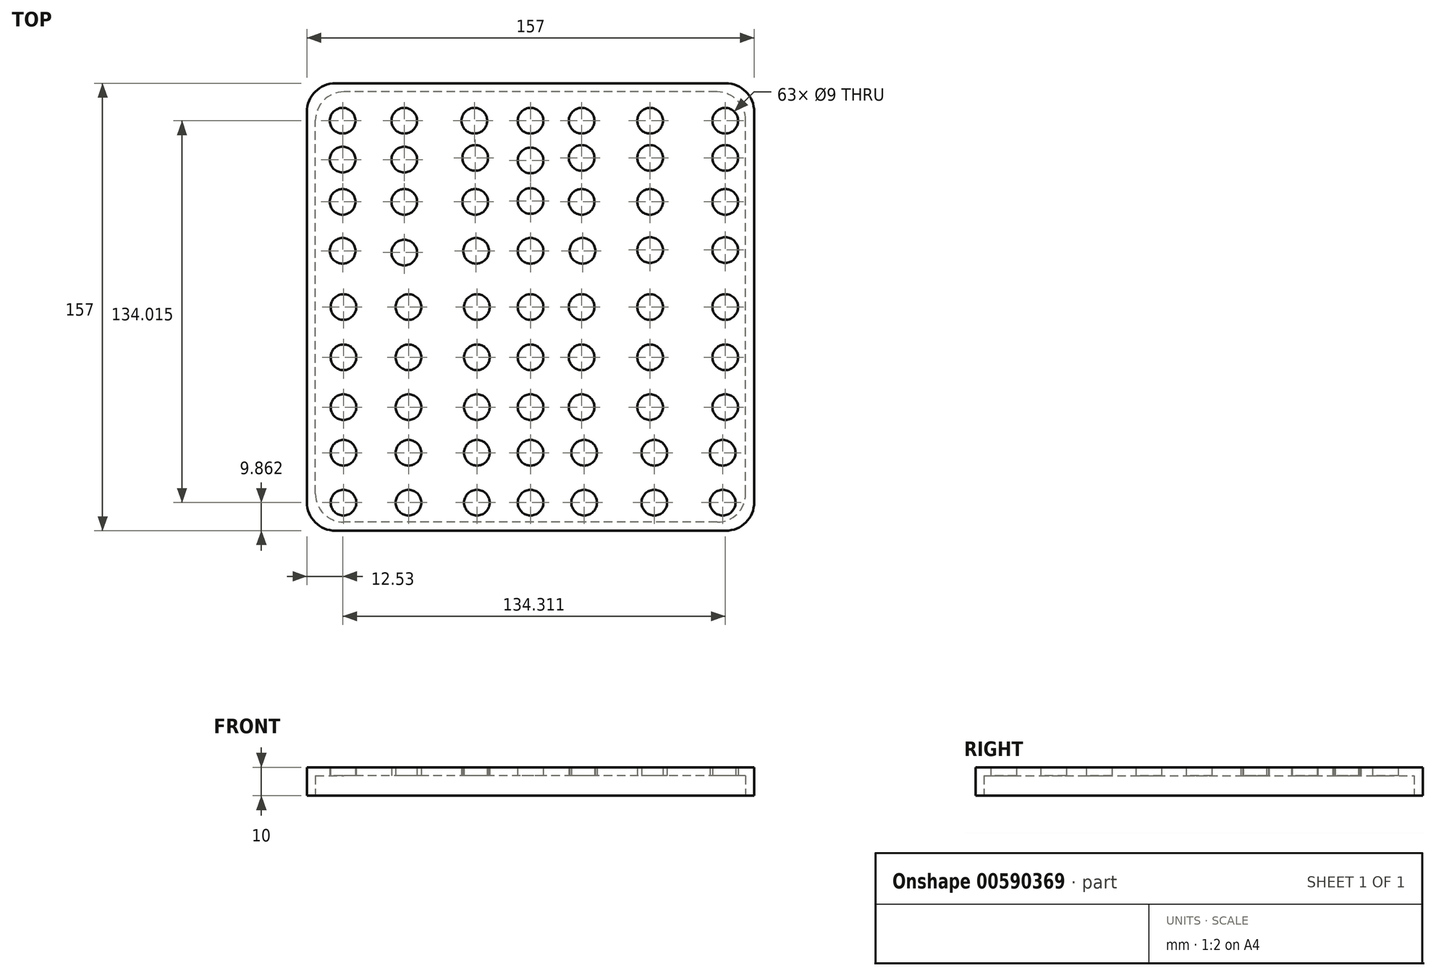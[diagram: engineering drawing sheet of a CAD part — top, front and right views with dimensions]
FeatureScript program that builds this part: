
annotation { "Feature Type Name" : "Feature", "Feature Type Description" : "" }
export const myFeature = defineFeature(function(context is Context, id is Id, definition is map)
    precondition{}
    {
        {
            var Q0;
            Q0=qCreatedBy(makeId("Top.planeOp"),FACE);
            var sketch = newSketch(context, id + "F0", { "sketchPlane" : qUnion([Q0])});
            skLineSegment(sketch, "E0.bottom", {"start": v(78.5, 78.5) * mm, "end": v(-78.5, 78.5) * mm});
            skLineSegment(sketch, "E0.top", {"start": v(78.5, -78.5) * mm, "end": v(-78.5, -78.5) * mm});
            skLineSegment(sketch, "E0.left", {"start": v(78.5, 78.5) * mm, "end": v(78.5, -78.5) * mm});
            skLineSegment(sketch, "E0.right", {"start": v(-78.5, 78.5) * mm, "end": v(-78.5, -78.5) * mm});
            skPoint(sketch, "E0.middle", {"position": v(0, 0) * mm});
            skSolve(sketch);
        }
        {
            var Q0;
            Q0=qSketchRegion(id+"F0",true);
            extrude(context, id + "F1", {"entities" : qUnion([Q0]), "depth" : 10 * mm, "offsetDistance" : 25 * mm});
        }
        {
            var Q0;
            Q0=qCreatedBy(makeId("Top.planeOp"),FACE);
            var sketch = newSketch(context, id + "F2", { "sketchPlane" : qUnion([Q0])});
            skLineSegment(sketch, "E1.bottom", {"start": v(75.5, -75.5) * mm, "end": v(-75.5, -75.5) * mm});
            skLineSegment(sketch, "E1.top", {"start": v(75.5, 75.5) * mm, "end": v(-75.5, 75.5) * mm});
            skLineSegment(sketch, "E1.left", {"start": v(75.5, -75.5) * mm, "end": v(75.5, 75.5) * mm});
            skLineSegment(sketch, "E1.right", {"start": v(-75.5, -75.5) * mm, "end": v(-75.5, 75.5) * mm});
            skSolve(sketch);
        }
        {
            var Q0;
            Q0=qSketchRegion(id+"F2",true);
            extrude(context, id + "F3", {"entities" : qUnion([Q0]), "operationType" : NewBodyOperationType.REMOVE, "depth" : 7 * mm, "offsetDistance" : 25 * mm});
        }
        {
            var Q0;
            Q0=qCreatedBy(makeId("Top.planeOp"),FACE);
            var sketch = newSketch(context, id + "F4", { "sketchPlane" : qUnion([Q0])});
            skPoint(sketch, "E2", {"position": v(0, 0) * mm});
            skPoint(sketch, "E3", {"position": v(0, 19.72) * mm});
            skPoint(sketch, "E4", {"position": v(0, 51.44) * mm});
            skPoint(sketch, "E5", {"position": v(0, 65.38) * mm});
            skPoint(sketch, "E6", {"position": v(0, 37.2) * mm});
            skPoint(sketch, "E7", {"position": v(17.94, 0) * mm});
            skPoint(sketch, "E8", {"position": v(41.95, 0) * mm});
            skPoint(sketch, "E9", {"position": v(68.34, 0) * mm});
            skPoint(sketch, "E10", {"position": v(-18.83, 0) * mm});
            skPoint(sketch, "E11", {"position": v(-42.84, 0) * mm});
            skPoint(sketch, "E12", {"position": v(-65.67, 0) * mm});
            skPoint(sketch, "E13", {"position": v(0, -17.64) * mm});
            skPoint(sketch, "E14", {"position": v(0, -35.13) * mm});
            skPoint(sketch, "E15", {"position": v(0, -51.15) * mm});
            skPoint(sketch, "E16", {"position": v(0, -68.64) * mm});
            skPoint(sketch, "E17", {"position": v(-44.33, 36.91) * mm});
            skPoint(sketch, "E18", {"position": v(-65.97, 65.38) * mm});
            skPoint(sketch, "E19", {"position": v(-44.33, 65.38) * mm});
            skPoint(sketch, "E20", {"position": v(-19.72, 65.38) * mm});
            skPoint(sketch, "E21", {"position": v(-44.33, 51.74) * mm});
            skPoint(sketch, "E22", {"position": v(-19.42, 52.33) * mm});
            skPoint(sketch, "E23", {"position": v(-19.42, 36.91) * mm});
            skPoint(sketch, "E24", {"position": v(-19.12, 19.72) * mm});
            skPoint(sketch, "E25", {"position": v(-44.33, 19.12) * mm});
            skPoint(sketch, "E26", {"position": v(-65.97, 36.91) * mm});
            skPoint(sketch, "E27", {"position": v(-65.97, 19.72) * mm});
            skPoint(sketch, "E28", {"position": v(-65.97, 51.74) * mm});
            skPoint(sketch, "E29", {"position": v(68.34, 20.01) * mm});
            skPoint(sketch, "E30", {"position": v(41.95, 20.01) * mm});
            skPoint(sketch, "E31", {"position": v(18.23, 19.72) * mm});
            skPoint(sketch, "E32", {"position": v(17.94, 36.91) * mm});
            skPoint(sketch, "E33", {"position": v(41.95, 36.91) * mm});
            skPoint(sketch, "E34", {"position": v(68.34, 36.91) * mm});
            skPoint(sketch, "E35", {"position": v(17.94, 65.38) * mm});
            skPoint(sketch, "E36", {"position": v(41.95, 65.38) * mm});
            skPoint(sketch, "E37", {"position": v(68.34, 65.38) * mm});
            skPoint(sketch, "E38", {"position": v(17.94, 52.33) * mm});
            skPoint(sketch, "E39", {"position": v(41.95, 52.33) * mm});
            skPoint(sketch, "E40", {"position": v(68.34, 52.33) * mm});
            skPoint(sketch, "E41", {"position": v(-18.83, -17.64) * mm});
            skPoint(sketch, "E42", {"position": v(-42.84, -17.64) * mm});
            skPoint(sketch, "E43", {"position": v(-65.67, -17.64) * mm});
            skPoint(sketch, "E44", {"position": v(-18.83, -35.13) * mm});
            skPoint(sketch, "E45", {"position": v(-42.84, -35.13) * mm});
            skPoint(sketch, "E46", {"position": v(-65.67, -35.13) * mm});
            skPoint(sketch, "E47", {"position": v(-18.83, -51.15) * mm});
            skPoint(sketch, "E48", {"position": v(-42.84, -51.15) * mm});
            skPoint(sketch, "E49", {"position": v(-65.67, -51.15) * mm});
            skPoint(sketch, "E50", {"position": v(-18.83, -68.64) * mm});
            skPoint(sketch, "E51", {"position": v(-42.84, -68.64) * mm});
            skPoint(sketch, "E52", {"position": v(-65.67, -68.64) * mm});
            skPoint(sketch, "E53", {"position": v(17.94, -17.64) * mm});
            skPoint(sketch, "E54", {"position": v(41.95, -17.64) * mm});
            skPoint(sketch, "E55", {"position": v(68.34, -17.64) * mm});
            skPoint(sketch, "E56", {"position": v(17.94, -35.13) * mm});
            skPoint(sketch, "E57", {"position": v(41.95, -35.13) * mm});
            skPoint(sketch, "E58", {"position": v(68.34, -35.13) * mm});
            skPoint(sketch, "E59", {"position": v(18.83, -51.15) * mm});
            skPoint(sketch, "E60", {"position": v(43.44, -51.15) * mm});
            skPoint(sketch, "E61", {"position": v(18.83, -68.64) * mm});
            skPoint(sketch, "E62", {"position": v(43.44, -68.64) * mm});
            skPoint(sketch, "E63", {"position": v(67.45, -51.15) * mm});
            skPoint(sketch, "E64", {"position": v(67.45, -68.64) * mm});
            skSolve(sketch);
        }
        {
            var Q0;
            Q0=sQuery(id+"F4.wireOp",VERTEX,"E2");
            var Q1;
            Q1=sQuery(id+"F4.wireOp",VERTEX,"01be2f64-9275-40fd-adfd-86fc247d9703");
            var Q2;
            Q2=sQuery(id+"F4.wireOp",VERTEX,"E3");
            var Q3;
            Q3=sQuery(id+"F4.wireOp",VERTEX,"E6");
            var Q4;
            Q4=sQuery(id+"F4.wireOp",VERTEX,"E4");
            var Q5;
            Q5=sQuery(id+"F4.wireOp",VERTEX,"E5");
            var Q6;
            Q6=sQuery(id+"F4.wireOp",VERTEX,"E7");
            var Q7;
            Q7=sQuery(id+"F4.wireOp",VERTEX,"7066c532-d9dd-423a-8bff-f60177c8eb84");
            var Q8;
            Q8=sQuery(id+"F4.wireOp",VERTEX,"E8");
            var Q9;
            Q9=sQuery(id+"F4.wireOp",VERTEX,"2cc3d04b-55ef-4e46-9bfc-cd6a145b7dbc");
            var Q10;
            Q10=sQuery(id+"F4.wireOp",VERTEX,"E9");
            var Q11;
            Q11=sQuery(id+"F4.wireOp",VERTEX,"E10");
            var Q12;
            Q12=sQuery(id+"F4.wireOp",VERTEX,"02460886-5748-4483-a859-1664056adb13");
            var Q13;
            Q13=sQuery(id+"F4.wireOp",VERTEX,"E11");
            var Q14;
            Q14=sQuery(id+"F4.wireOp",VERTEX,"182e11dd-57cf-4a7e-8525-31e6d83ff862");
            var Q15;
            Q15=sQuery(id+"F4.wireOp",VERTEX,"E12");
            var Q16;
            Q16=sQuery(id+"F4.wireOp",VERTEX,"E13");
            var Q17;
            Q17=sQuery(id+"F4.wireOp",VERTEX,"E14");
            var Q18;
            Q18=sQuery(id+"F4.wireOp",VERTEX,"22c52a95-364c-45c8-bfcc-b8bc63de801a");
            var Q19;
            Q19=sQuery(id+"F4.wireOp",VERTEX,"E15");
            var Q20;
            Q20=sQuery(id+"F4.wireOp",VERTEX,"c324e29c-9176-4c9c-977c-a24ceaadd785");
            var Q21;
            Q21=sQuery(id+"F4.wireOp",VERTEX,"92aa8679-3bd7-4545-9122-d12983432420");
            var Q22;
            Q22=sQuery(id+"F4.wireOp",VERTEX,"E33");
            var Q23;
            Q23=sQuery(id+"F4.wireOp",VERTEX,"96c0b8bc-8c1f-43fb-ba5c-182eb7d20bf4");
            var Q24;
            Q24=sQuery(id+"F4.wireOp",VERTEX,"E37");
            var Q25;
            Q25=sQuery(id+"F4.wireOp",VERTEX,"E40");
            var Q26;
            Q26=sQuery(id+"F4.wireOp",VERTEX,"E34");
            var Q27;
            Q27=sQuery(id+"F4.wireOp",VERTEX,"c3c9688b-514f-4bd6-b36d-9f046526faeb");
            var Q28;
            Q28=sQuery(id+"F4.wireOp",VERTEX,"48e804fb-e4a2-4aba-a25b-484107231475");
            var Q29;
            Q29=sQuery(id+"F4.wireOp",VERTEX,"E29");
            var Q30;
            Q30=sQuery(id+"F4.wireOp",VERTEX,"74c768e5-57bc-481c-99f9-a4891877f862");
            var Q31;
            Q31=sQuery(id+"F4.wireOp",VERTEX,"a0b9cffa-d664-4735-8a3a-198f2cd382f6");
            var Q32;
            Q32=sQuery(id+"F4.wireOp",VERTEX,"56d23400-79b2-4586-ace4-7da2e45eed59");
            var Q33;
            Q33=sQuery(id+"F4.wireOp",VERTEX,"E31");
            var Q34;
            Q34=sQuery(id+"F4.wireOp",VERTEX,"E32");
            var Q35;
            Q35=sQuery(id+"F4.wireOp",VERTEX,"f03c099e-2c18-4fb1-a7fd-04fbad21f07c");
            var Q36;
            Q36=sQuery(id+"F4.wireOp",VERTEX,"551dea10-b2b5-4e0e-ad8b-eb0ab3a4bef2");
            var Q37;
            Q37=sQuery(id+"F4.wireOp",VERTEX,"E39");
            var Q38;
            Q38=sQuery(id+"F4.wireOp",VERTEX,"E36");
            var Q39;
            Q39=sQuery(id+"F4.wireOp",VERTEX,"7103e156-cc1c-4737-8f98-ad15fd8e018d");
            var Q40;
            Q40=sQuery(id+"F4.wireOp",VERTEX,"6184139e-c808-43f1-a726-8d870d67d640");
            var Q41;
            Q41=sQuery(id+"F4.wireOp",VERTEX,"E38");
            var Q42;
            Q42=sQuery(id+"F4.wireOp",VERTEX,"E20");
            var Q43;
            Q43=sQuery(id+"F4.wireOp",VERTEX,"1f5d0829-9c7d-4bc5-9e43-8e9a9d462987");
            var Q44;
            Q44=sQuery(id+"F4.wireOp",VERTEX,"E18");
            var Q45;
            Q45=sQuery(id+"F4.wireOp",VERTEX,"E35");
            var Q46;
            Q46=sQuery(id+"F4.wireOp",VERTEX,"8592a42e-3bac-4ad7-8a0c-d7e574435690");
            var Q47;
            Q47=sQuery(id+"F4.wireOp",VERTEX,"E30");
            var Q48;
            Q48=sQuery(id+"F4.wireOp",VERTEX,"E22");
            var Q49;
            Q49=sQuery(id+"F4.wireOp",VERTEX,"E23");
            var Q50;
            Q50=sQuery(id+"F4.wireOp",VERTEX,"E24");
            var Q51;
            Q51=sQuery(id+"F4.wireOp",VERTEX,"3a65e8a7-9de3-45d0-bf0d-3870d7435693");
            var Q52;
            Q52=sQuery(id+"F4.wireOp",VERTEX,"a2867e8b-1ec6-4e94-be05-c84491770e30");
            var Q53;
            Q53=sQuery(id+"F4.wireOp",VERTEX,"74bc8962-0474-4ee7-b79d-48d9b9152ced");
            var Q54;
            Q54=sQuery(id+"F4.wireOp",VERTEX,"7c793132-c5a2-48cd-879b-69ca076af330");
            var Q55;
            Q55=sQuery(id+"F4.wireOp",VERTEX,"d544b1af-dadb-42ff-aaa4-5aa6b3774210");
            var Q56;
            Q56=sQuery(id+"F4.wireOp",VERTEX,"E27");
            var Q57;
            Q57=sQuery(id+"F4.wireOp",VERTEX,"E26");
            var Q58;
            Q58=sQuery(id+"F4.wireOp",VERTEX,"E28");
            var Q59;
            Q59=sQuery(id+"F4.wireOp",VERTEX,"01be4d33-b820-451f-a3cf-1a212500c26a");
            var Q60;
            Q60=sQuery(id+"F4.wireOp",VERTEX,"E21");
            var Q61;
            Q61=sQuery(id+"F4.wireOp",VERTEX,"1b0218f6-6790-4433-853d-df34f0919a04");
            var Q62;
            Q62=sQuery(id+"F4.wireOp",VERTEX,"34c218e5-a3b0-42ed-8128-703f8c3a5e80");
            var Q63;
            Q63=sQuery(id+"F4.wireOp",VERTEX,"E17");
            var Q64;
            Q64=sQuery(id+"F4.wireOp",VERTEX,"f6e993d7-34cf-4690-b225-ecafc0a23a5c");
            var Q65;
            Q65=sQuery(id+"F4.wireOp",VERTEX,"f4d6c966-a790-413c-ac3a-f2849b012799");
            var Q66;
            Q66=sQuery(id+"F4.wireOp",VERTEX,"E25");
            var Q67;
            Q67=sQuery(id+"F4.wireOp",VERTEX,"cba1d7b0-17a4-442b-8538-578cc5b2ca6f");
            var Q68;
            Q68=sQuery(id+"F4.wireOp",VERTEX,"E19");
            var Q69;
            Q69=sQuery(id+"F4.wireOp",VERTEX,"03945a85-c6ad-43cf-af4f-6afe4fa288b2");
            var Q70;
            Q70=sQuery(id+"F4.wireOp",VERTEX,"7290b2f6-eeda-4de9-9caa-206615dc3dbb");
            var Q71;
            Q71=sQuery(id+"F4.wireOp",VERTEX,"26922496-9d20-4b5e-a89f-083a322c1987");
            var Q72;
            Q72=sQuery(id+"F4.wireOp",VERTEX,"48f5341c-4d69-4476-84ce-7808d27898a8");
            var Q73;
            Q73=sQuery(id+"F4.wireOp",VERTEX,"95d1ae6e-98a4-43e9-aa43-69d7da4bf474");
            var Q74;
            Q74=sQuery(id+"F4.wireOp",VERTEX,"c13eeef2-ced9-4608-8eb4-db277dc040c4");
            var Q75;
            Q75=sQuery(id+"F4.wireOp",VERTEX,"E52");
            var Q76;
            Q76=sQuery(id+"F4.wireOp",VERTEX,"E49");
            var Q77;
            Q77=sQuery(id+"F4.wireOp",VERTEX,"084463ea-29c9-4709-b3b4-8312bc72499e");
            var Q78;
            Q78=sQuery(id+"F4.wireOp",VERTEX,"E46");
            var Q79;
            Q79=sQuery(id+"F4.wireOp",VERTEX,"E43");
            var Q80;
            Q80=sQuery(id+"F4.wireOp",VERTEX,"E42");
            var Q81;
            Q81=sQuery(id+"F4.wireOp",VERTEX,"E45");
            var Q82;
            Q82=sQuery(id+"F4.wireOp",VERTEX,"2d919faf-3943-4703-a885-04c4fa0d63f4");
            var Q83;
            Q83=sQuery(id+"F4.wireOp",VERTEX,"487494f3-2b61-4049-9145-c1a29d6889ac");
            var Q84;
            Q84=sQuery(id+"F4.wireOp",VERTEX,"E44");
            var Q85;
            Q85=sQuery(id+"F4.wireOp",VERTEX,"E41");
            var Q86;
            Q86=sQuery(id+"F4.wireOp",VERTEX,"90ec04d7-373d-4612-91dc-7855c4c59f71");
            var Q87;
            Q87=sQuery(id+"F4.wireOp",VERTEX,"46c18770-5906-4691-aaab-63a2d037b7b3");
            var Q88;
            Q88=sQuery(id+"F4.wireOp",VERTEX,"34362282-205a-428d-81e4-b473148326ca");
            var Q89;
            Q89=sQuery(id+"F4.wireOp",VERTEX,"E51");
            var Q90;
            Q90=sQuery(id+"F4.wireOp",VERTEX,"37bfcbe4-644b-4fb2-b4e6-cfaa0b7adfe0");
            var Q91;
            Q91=sQuery(id+"F4.wireOp",VERTEX,"E50");
            var Q92;
            Q92=sQuery(id+"F4.wireOp",VERTEX,"E47");
            var Q93;
            Q93=sQuery(id+"F4.wireOp",VERTEX,"5aa79f74-e0c4-402e-b933-62c2ee8fbe12");
            var Q94;
            Q94=sQuery(id+"F4.wireOp",VERTEX,"E59");
            var Q95;
            Q95=sQuery(id+"F4.wireOp",VERTEX,"b110cdba-c84a-4cd0-a5ab-248e47baa77b");
            var Q96;
            Q96=sQuery(id+"F4.wireOp",VERTEX,"E56");
            var Q97;
            Q97=sQuery(id+"F4.wireOp",VERTEX,"E53");
            var Q98;
            Q98=sQuery(id+"F4.wireOp",VERTEX,"41f0f1f3-9fe2-4819-9743-bab9cb15a025");
            var Q99;
            Q99=sQuery(id+"F4.wireOp",VERTEX,"E54");
            var Q100;
            Q100=sQuery(id+"F4.wireOp",VERTEX,"a45bf8b3-a4b9-474f-a59b-51bde7ee29a6");
            var Q101;
            Q101=sQuery(id+"F4.wireOp",VERTEX,"E55");
            var Q102;
            Q102=sQuery(id+"F4.wireOp",VERTEX,"E58");
            var Q103;
            Q103=sQuery(id+"F4.wireOp",VERTEX,"3c85369c-51f2-47f6-b650-f701993649a4");
            var Q104;
            Q104=sQuery(id+"F4.wireOp",VERTEX,"E57");
            var Q105;
            Q105=sQuery(id+"F4.wireOp",VERTEX,"8a02a5f6-1d99-4ddf-979c-71fcefaade30");
            var Q106;
            Q106=sQuery(id+"F4.wireOp",VERTEX,"E60");
            var Q107;
            Q107=sQuery(id+"F4.wireOp",VERTEX,"f2076d12-8ec6-4e44-a1c4-b4ed78cc275c");
            var Q108;
            Q108=sQuery(id+"F4.wireOp",VERTEX,"7f2df35a-0d4d-4b3b-84d0-fbce83f4655d");
            var Q109;
            Q109=sQuery(id+"F4.wireOp",VERTEX,"0c621542-6388-4c85-b89b-5a6bf10c55ee");
            var Q110;
            Q110=sQuery(id+"F4.wireOp",VERTEX,"E61");
            var Q111;
            Q111=sQuery(id+"F4.wireOp",VERTEX,"E16");
            var Q112;
            Q112=sQuery(id+"F4.wireOp",VERTEX,"E62");
            var Q113;
            Q113=sQuery(id+"F4.wireOp",VERTEX,"dd011270-05db-4ea7-b964-71307e0b1595");
            var Q114;
            Q114=sQuery(id+"F4.wireOp",VERTEX,"E64");
            var Q115;
            Q115=sQuery(id+"F4.wireOp",VERTEX,"5a7bd326-e4b6-442a-b6d6-203f70899100");
            var Q116;
            Q116=sQuery(id+"F4.wireOp",VERTEX,"fdff5e05-710b-4cf5-88a8-f8bf924db13f");
            var Q117;
            Q117=sQuery(id+"F4.wireOp",VERTEX,"bc33214d-c343-44b5-bf20-2491ec213792");
            var Q118;
            Q118=sQuery(id+"F4.wireOp",VERTEX,"E63");
            var Q119;
            Q119=sQuery(id+"F4.wireOp",VERTEX,"ed207939-6ef3-43b8-a54d-e9702f4834c8");
            var Q120;
            Q120=sQuery(id+"F4.wireOp",VERTEX,"E48");
            var Q121;
            Q121=makeQuery(id+"F1.opExtrude","SWEPT_BODY",BODY,{"disambiguationData":[OSD([sQuery(id+"F0.wireOp",EDGE,"E0.bottom"),sQuery(id+"F0.wireOp",EDGE,"E0.top"),sQuery(id+"F0.wireOp",EDGE,"E0.left"),sQuery(id+"F0.wireOp",EDGE,"E0.right")])]});
            hole(context, id + "F5", {"style" : HoleStyle.C_SINK, "endStyle" : HoleEndStyle.THROUGH, "oppositeDirection" : true, "holeDiameter" : 9 * mm, "cSinkDiameter" : 10 * mm, "cSinkAngle" : 90 * degree, "majorDiameter" : 5 * mm, "isTappedThrough" : true, "tappedDepth" : 12 * mm, "tapClearance" : 3, "startFromSketch" : true, "locations" : qUnion([Q0, Q1, Q2, Q3, Q4, Q5, Q6, Q7, Q8, Q9, Q10, Q11, Q12, Q13, Q14, Q15, Q16, Q17, Q18, Q19, Q20, Q21, Q22, Q23, Q24, Q25, Q26, Q27, Q28, Q29, Q30, Q31, Q32, Q33, Q34, Q35, Q36, Q37, Q38, Q39, Q40, Q41, Q42, Q43, Q44, Q45, Q46, Q47, Q48, Q49, Q50, Q51, Q52, Q53, Q54, Q55, Q56, Q57, Q58, Q59, Q60, Q61, Q62, Q63, Q64, Q65, Q66, Q67, Q68, Q69, Q70, Q71, Q72, Q73, Q74, Q75, Q76, Q77, Q78, Q79, Q80, Q81, Q82, Q83, Q84, Q85, Q86, Q87, Q88, Q89, Q90, Q91, Q92, Q93, Q94, Q95, Q96, Q97, Q98, Q99, Q100, Q101, Q102, Q103, Q104, Q105, Q106, Q107, Q108, Q109, Q110, Q111, Q112, Q113, Q114, Q115, Q116, Q117, Q118, Q119, Q120]), "scope" : qUnion([Q121])});
        }
        {
            var Q0;
            Q0=makeQuery(id+"F1.opExtrude","SWEPT_EDGE",EDGE,{"disambiguationData":[OSD([sQuery(id+"F0.wireOp",EDGE,"E0.bottom"),sQuery(id+"F0.wireOp",EDGE,"E0.left")])]});
            var Q1;
            Q1=makeQuery(id+"F1.opExtrude","SWEPT_EDGE",EDGE,{"disambiguationData":[OSD([sQuery(id+"F0.wireOp",EDGE,"E0.bottom"),sQuery(id+"F0.wireOp",EDGE,"E0.right")])]});
            var Q2;
            Q2=makeQuery(id+"F1.opExtrude","SWEPT_EDGE",EDGE,{"disambiguationData":[OSD([sQuery(id+"F0.wireOp",EDGE,"E0.top"),sQuery(id+"F0.wireOp",EDGE,"E0.left")])]});
            fillet(context, id + "F6", {"entities" : qUnion([Q0, Q1, Q2]), "radius" : 10 * mm, "tangentPropagation" : true, "allowEdgeOverflow" : false});
        }
        {
            var Q0;
            Q0=makeQuery(id+"F1.opExtrude","SWEPT_EDGE",EDGE,{"disambiguationData":[OSD([sQuery(id+"F0.wireOp",EDGE,"E0.top"),sQuery(id+"F0.wireOp",EDGE,"E0.right")])]});
            fillet(context, id + "F7", {"entities" : qUnion([Q0]), "radius" : 10 * mm, "tangentPropagation" : true, "allowEdgeOverflow" : false});
        }
        {
            var Q0;
            Q0=makeQuery(id+"F3.boolean.opBoolean","COPY",EDGE,{"derivedFrom":makeQuery(id+"F3.opExtrude","SWEPT_EDGE",EDGE,{"disambiguationData":[OSD([sQuery(id+"F2.wireOp",EDGE,"E1.bottom"),sQuery(id+"F2.wireOp",EDGE,"E1.left")])]})});
            var Q1;
            Q1=makeQuery(id+"F3.boolean.opBoolean","COPY",EDGE,{"derivedFrom":makeQuery(id+"F3.opExtrude","SWEPT_EDGE",EDGE,{"disambiguationData":[OSD([sQuery(id+"F2.wireOp",EDGE,"E1.bottom"),sQuery(id+"F2.wireOp",EDGE,"E1.right")])]})});
            var Q2;
            Q2=makeQuery(id+"F3.boolean.opBoolean","COPY",EDGE,{"derivedFrom":makeQuery(id+"F3.opExtrude","SWEPT_EDGE",EDGE,{"disambiguationData":[OSD([sQuery(id+"F2.wireOp",EDGE,"E1.top"),sQuery(id+"F2.wireOp",EDGE,"E1.right")])]})});
            var Q3;
            Q3=makeQuery(id+"F3.boolean.opBoolean","COPY",EDGE,{"derivedFrom":makeQuery(id+"F3.opExtrude","SWEPT_EDGE",EDGE,{"disambiguationData":[OSD([sQuery(id+"F2.wireOp",EDGE,"E1.top"),sQuery(id+"F2.wireOp",EDGE,"E1.left")])]})});
            fillet(context, id + "F8", {"entities" : qUnion([Q0, Q1, Q2, Q3]), "radius" : 10 * mm, "tangentPropagation" : true, "allowEdgeOverflow" : false});
        }
    });
